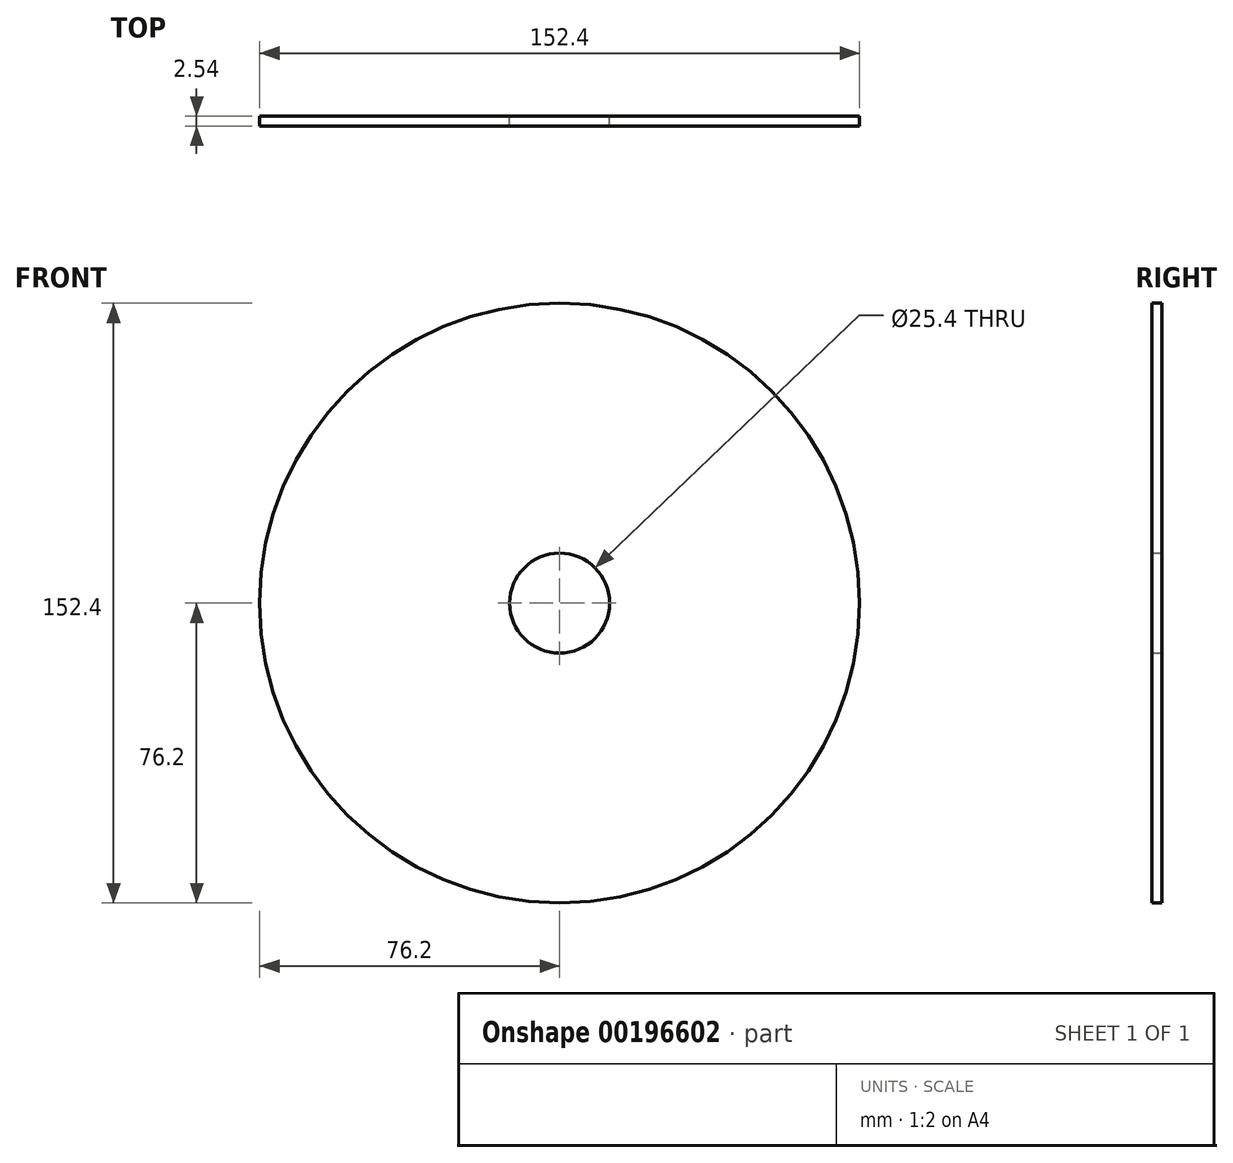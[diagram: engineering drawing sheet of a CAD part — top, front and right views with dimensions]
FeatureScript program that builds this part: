
annotation { "Feature Type Name" : "Feature", "Feature Type Description" : "" }
export const myFeature = defineFeature(function(context is Context, id is Id, definition is map)
    precondition{}
    {
        {
            var Q0;
            Q0=qCreatedBy(makeId("Front.planeOp"),FACE);
            var sketch = newSketch(context, id + "F0", { "sketchPlane" : qUnion([Q0])});
            skCircle(sketch, "E0", {"center": v(0, 0) * mm, "radius": 76.2 * mm});
            skSolve(sketch);
        }
        {
            var Q0;
            Q0=makeQuery(id+"F0.imprint","IMPRINT",FACE,{"disambiguationData":[TD([[makeQuery(id+"F0.imprint","IMPRINT",EDGE,{"derivedFrom":sQuery(id+"F0.wireOp",EDGE,"E0")}),1.0]])]});
            extrude(context, id + "F1", {"entities" : qUnion([Q0]), "depth" : 2.54 * mm, "offsetDistance" : 25.4 * mm});
        }
        {
            var Q0;
            Q0=qCreatedBy(makeId("Front.planeOp"),FACE);
            var sketch = newSketch(context, id + "F2", { "sketchPlane" : qUnion([Q0])});
            skCircle(sketch, "E1", {"center": v(0, 0) * mm, "radius": 12.7 * mm});
            skSolve(sketch);
        }
        {
            var Q0;
            Q0 = qSketchRegion(id + "F2", true);
            extrude(context, id + "F3", {"entities" : qUnion([Q0]), "operationType" : NewBodyOperationType.REMOVE, "oppositeDirection" : true, "depth" : -2.54 * mm, "offsetDistance" : 25.4 * mm});
        }
    });
